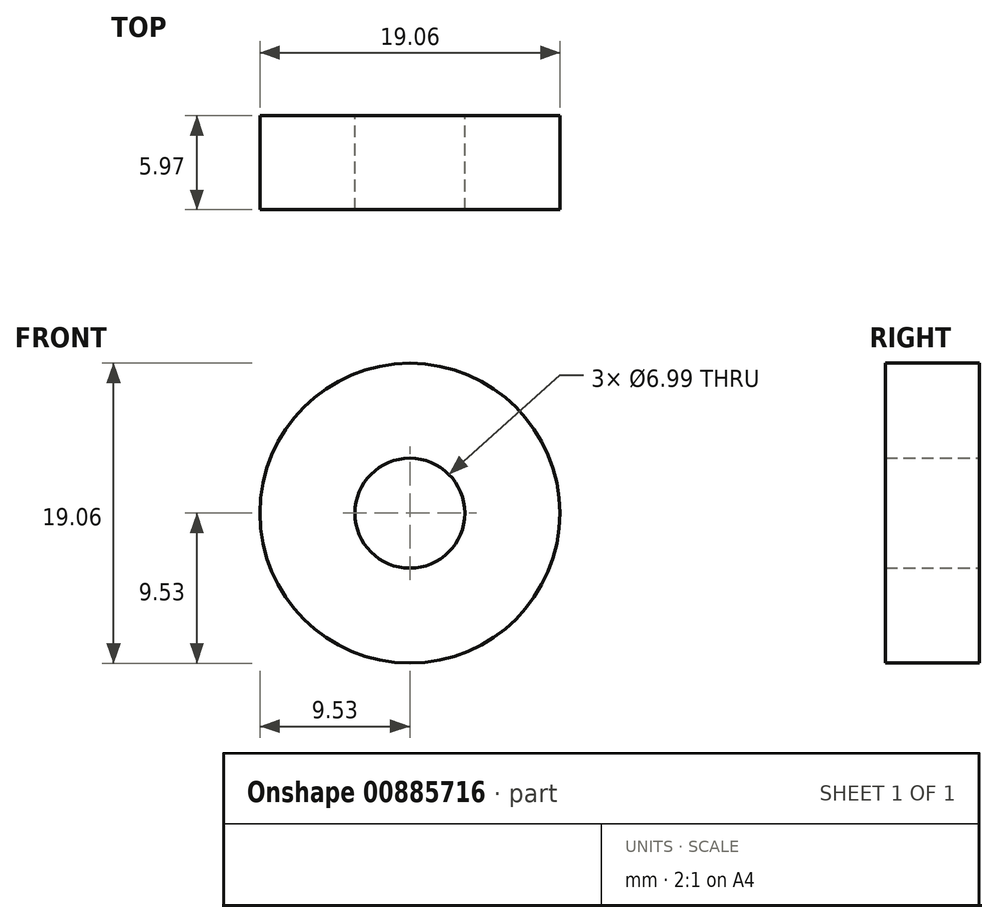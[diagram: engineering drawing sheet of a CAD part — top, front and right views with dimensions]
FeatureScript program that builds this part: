
annotation { "Feature Type Name" : "Feature", "Feature Type Description" : "" }
export const myFeature = defineFeature(function(context is Context, id is Id, definition is map)
    precondition{}
    {
        {
            var Q0;
            Q0=qCreatedBy(makeId("Front.planeOp"),FACE);
            var sketch = newSketch(context, id + "F0", { "sketchPlane" : qUnion([Q0])});
            skCircle(sketch, "E0", {"center": v(0, 0) * mm, "radius": 3.5 * mm});
            skCircle(sketch, "E1", {"center": v(0, 0) * mm, "radius": 9.53 * mm});
            skSolve(sketch);
        }
        {
            var Q0;
            Q0 = qSketchRegion(id + "F0", true);
            extrude(context, id + "F1", {"entities" : qUnion([Q0]), "depth" : 5.97 * mm, "offsetDistance" : 25.4 * mm});
        }
    });
